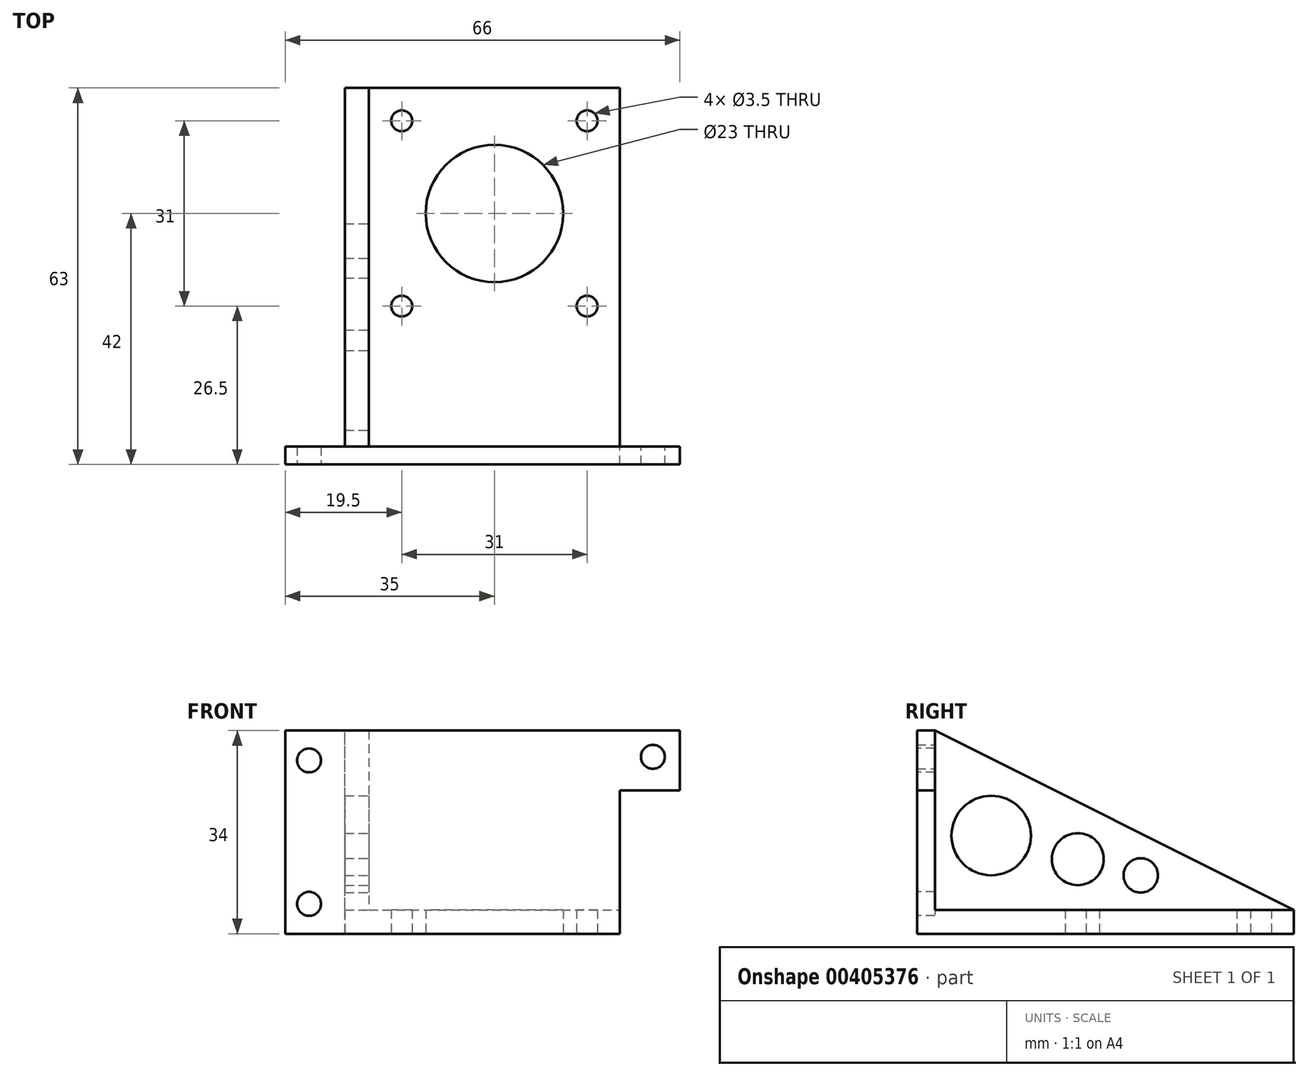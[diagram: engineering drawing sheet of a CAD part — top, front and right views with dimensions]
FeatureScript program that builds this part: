
annotation { "Feature Type Name" : "Feature", "Feature Type Description" : "" }
export const myFeature = defineFeature(function(context is Context, id is Id, definition is map)
    precondition{}
    {
        {
            var Q0;
            Q0=qCreatedBy(makeId("Top.planeOp"),FACE);
            var sketch = newSketch(context, id + "F0", { "sketchPlane" : qUnion([Q0])});
            skLineSegment(sketch, "E0.bottom", {"start": v(-21, 31.5) * mm, "end": v(21, 31.5) * mm});
            skLineSegment(sketch, "E0.top", {"start": v(-21, -31.5) * mm, "end": v(21, -31.5) * mm});
            skLineSegment(sketch, "E0.left", {"start": v(-21, 31.5) * mm, "end": v(-21, -31.5) * mm});
            skLineSegment(sketch, "E0.right", {"start": v(21, 31.5) * mm, "end": v(21, -31.5) * mm});
            skPoint(sketch, "E0.middle", {"position": v(0, 0) * mm});
            skCircle(sketch, "E1", {"center": v(0, 10.5) * mm, "radius": 11.5 * mm});
            skCircle(sketch, "E2", {"center": v(-15.5, 26) * mm, "radius": 1.75 * mm});
            skCircle(sketch, "E3.1.0", {"center": v(-15.5, -5) * mm, "radius": 1.75 * mm});
            skCircle(sketch, "E3.2.0", {"center": v(15.5, -5) * mm, "radius": 1.75 * mm});
            skCircle(sketch, "E3.3.0", {"center": v(15.5, 26) * mm, "radius": 1.75 * mm});
            skSolve(sketch);
        }
        {
            var Q0;
            Q0=makeQuery(id+"F0.imprint","IMPRINT",FACE,{"disambiguationData":[TD([[makeQuery(id+"F0.imprint","IMPRINT",EDGE,{"derivedFrom":sQuery(id+"F0.wireOp",EDGE,"E0.bottom")}),-1.0]])]});
            extrude(context, id + "F1", {"entities" : qUnion([Q0]), "depth" : 4 * mm});
        }
        {
            var Q0;
            Q0=makeQuery(id+"F1.opExtrude","CAP_FACE",FACE,{"disambiguationData":[OSD([sQuery(id+"F0.wireOp",EDGE,"E0.bottom"),sQuery(id+"F0.wireOp",EDGE,"E0.top"),sQuery(id+"F0.wireOp",EDGE,"E0.left"),sQuery(id+"F0.wireOp",EDGE,"E0.right"),sQuery(id+"F0.wireOp",EDGE,"E1"),sQuery(id+"F0.wireOp",EDGE,"E2"),sQuery(id+"F0.wireOp",EDGE,"E3.1.0"),sQuery(id+"F0.wireOp",EDGE,"E3.2.0"),sQuery(id+"F0.wireOp",EDGE,"E3.3.0")])],"isStart":false});
            var sketch = newSketch(context, id + "F2", { "sketchPlane" : qUnion([Q0])});
            skLineSegment(sketch, "E4.bottom", {"start": v(-21, -31.5) * mm, "end": v(21, -31.5) * mm});
            skLineSegment(sketch, "E4.top", {"start": v(-21, -28.5) * mm, "end": v(21, -28.5) * mm});
            skLineSegment(sketch, "E4.left", {"start": v(-21, -31.5) * mm, "end": v(-21, -28.5) * mm});
            skLineSegment(sketch, "E4.right", {"start": v(21, -31.5) * mm, "end": v(21, -28.5) * mm});
            skSolve(sketch);
        }
        {
            var Q0;
            Q0=makeQuery(id+"F2.imprint","IMPRINT",FACE,{"disambiguationData":[TD([[makeQuery(id+"F2.imprint","IMPRINT",EDGE,{"derivedFrom":sQuery(id+"F2.wireOp",EDGE,"E4.bottom")}),1.0]])]});
            extrude(context, id + "F3", {"entities" : qUnion([Q0]), "operationType" : NewBodyOperationType.ADD, "depth" : 30 * mm});
        }
        {
            var Q0;
            Q0=makeQuery(id+"F3.boolean.opBoolean","MERGE",FACE,{"derivedFrom":[makeQuery(id+"F1.opExtrude","SWEPT_FACE",FACE,{"disambiguationData":[OSD([sQuery(id+"F0.wireOp",EDGE,"E0.left")])]}),makeQuery(id+"F3.opExtrude","SWEPT_FACE",FACE,{"disambiguationData":[OSD([sQuery(id+"F2.wireOp",EDGE,"E4.left")])]})]});
            var sketch = newSketch(context, id + "F4", { "sketchPlane" : qUnion([Q0])});
            skLineSegment(sketch, "E5", {"start": v(-31.5, 4) * mm, "end": v(28.5, 34) * mm});
            skLineSegment(sketch, "E6", {"start": v(28.5, 34) * mm, "end": v(31.5, 34) * mm});
            skLineSegment(sketch, "E7", {"start": v(31.5, 34) * mm, "end": v(31.5, 0) * mm});
            skLineSegment(sketch, "E8", {"start": v(31.5, 0) * mm, "end": v(-31.5, 0) * mm});
            skLineSegment(sketch, "E9", {"start": v(-31.5, 0) * mm, "end": v(-31.5, 4) * mm});
            skCircle(sketch, "E10", {"center": v(19.1, 16.43) * mm, "radius": 6.65 * mm});
            skCircle(sketch, "E11", {"center": v(4.62, 12.47) * mm, "radius": 4.34 * mm});
            skCircle(sketch, "E12", {"center": v(-5.9, 9.76) * mm, "radius": 2.88 * mm});
            skSolve(sketch);
        }
        {
            var Q0;
            Q0=makeQuery(id+"F4.imprint","IMPRINT",FACE,{"disambiguationData":[TD([[makeQuery(id+"F4.imprint","IMPRINT",EDGE,{"derivedFrom":sQuery(id+"F4.wireOp",EDGE,"E5")}),-1.0]])]});
            var Q1;
            Q1=makeQuery(id+"F4.imprint","IMPRINT",FACE,{"disambiguationData":[TD([[makeQuery(id+"F4.imprint","IMPRINT",EDGE,{"derivedFrom":sQuery(id+"F4.wireOp",EDGE,"E6")}),-1.0]])]});
            extrude(context, id + "F5", {"entities" : qUnion([Q0, Q1]), "operationType" : NewBodyOperationType.ADD, "depth" : 4 * mm});
        }
        {
            var Q0;
            Q0=makeQuery(id+"F3.boolean.opBoolean","MERGE",FACE,{"derivedFrom":[makeQuery(id+"F1.opExtrude","SWEPT_FACE",FACE,{"disambiguationData":[OSD([sQuery(id+"F0.wireOp",EDGE,"E0.right")])]}),makeQuery(id+"F3.opExtrude","SWEPT_FACE",FACE,{"disambiguationData":[OSD([sQuery(id+"F2.wireOp",EDGE,"E4.right")])]})]});
            var sketch = newSketch(context, id + "F6", { "sketchPlane" : qUnion([Q0])});
            skLineSegment(sketch, "E13.bottom", {"start": v(-31.5, 34) * mm, "end": v(-28.5, 34) * mm});
            skLineSegment(sketch, "E13.top", {"start": v(-31.5, 24) * mm, "end": v(-28.5, 24) * mm});
            skLineSegment(sketch, "E13.left", {"start": v(-31.5, 34) * mm, "end": v(-31.5, 24) * mm});
            skLineSegment(sketch, "E13.right", {"start": v(-28.5, 34) * mm, "end": v(-28.5, 24) * mm});
            skSolve(sketch);
        }
        {
            var Q0;
            Q0=makeQuery(id+"F6.imprint","IMPRINT",FACE,{"disambiguationData":[TD([[makeQuery(id+"F6.imprint","IMPRINT",EDGE,{"derivedFrom":sQuery(id+"F6.wireOp",EDGE,"E13.bottom")}),1.0]])]});
            extrude(context, id + "F7", {"entities" : qUnion([Q0]), "operationType" : NewBodyOperationType.ADD, "depth" : 10 * mm});
        }
        {
            var Q0;
            Q0=makeQuery(id+"F7.boolean.opBoolean","MERGE",FACE,{"derivedFrom":[makeQuery(id+"F3.opExtrude","SWEPT_FACE",FACE,{"disambiguationData":[OSD([sQuery(id+"F2.wireOp",EDGE,"E4.top")])]}),makeQuery(id+"F7.opExtrude","SWEPT_FACE",FACE,{"disambiguationData":[OSD([sQuery(id+"F6.wireOp",EDGE,"E13.right")])]})]});
            var sketch = newSketch(context, id + "F8", { "sketchPlane" : qUnion([Q0])});
            skCircle(sketch, "E14", {"center": v(-26.5, 29.6) * mm, "radius": 2 * mm});
            skSolve(sketch);
        }
        {
            var Q0;
            Q0=makeQuery(id+"F8.imprint","IMPRINT",FACE,{"disambiguationData":[TD([[makeQuery(id+"F8.imprint","IMPRINT",EDGE,{"derivedFrom":sQuery(id+"F8.wireOp",EDGE,"E14")}),1.0]])]});
            extrude(context, id + "F9", {"entities" : qUnion([Q0]), "operationType" : NewBodyOperationType.REMOVE, "oppositeDirection" : true, "depth" : 25 * mm});
        }
        {
            var Q0;
            Q0=makeQuery(id+"F5.opExtrude","CAP_FACE",FACE,{"disambiguationData":[OSD([sQuery(id+"F4.wireOp",EDGE,"E5"),sQuery(id+"F4.wireOp",EDGE,"E6"),sQuery(id+"F4.wireOp",EDGE,"E7"),sQuery(id+"F4.wireOp",EDGE,"E8"),sQuery(id+"F4.wireOp",EDGE,"E9"),sQuery(id+"F4.wireOp",EDGE,"E10"),sQuery(id+"F4.wireOp",EDGE,"E11"),sQuery(id+"F4.wireOp",EDGE,"E12")])],"isStart":false});
            var sketch = newSketch(context, id + "F10", { "sketchPlane" : qUnion([Q0])});
            skLineSegment(sketch, "E15.bottom", {"start": v(31.5, 0) * mm, "end": v(28.5, 0) * mm});
            skLineSegment(sketch, "E15.top", {"start": v(31.5, 34) * mm, "end": v(28.5, 34) * mm});
            skLineSegment(sketch, "E15.left", {"start": v(31.5, 0) * mm, "end": v(31.5, 34) * mm});
            skLineSegment(sketch, "E15.right", {"start": v(28.5, 0) * mm, "end": v(28.5, 34) * mm});
            skSolve(sketch);
        }
        {
            var Q0;
            Q0=makeQuery(id+"F10.imprint","IMPRINT",FACE,{"disambiguationData":[TD([[makeQuery(id+"F10.imprint","IMPRINT",EDGE,{"derivedFrom":sQuery(id+"F10.wireOp",EDGE,"E15.bottom")}),1.0]])]});
            extrude(context, id + "F11", {"entities" : qUnion([Q0]), "operationType" : NewBodyOperationType.ADD, "depth" : 10 * mm});
        }
        {
            var Q0;
            Q0=makeQuery(id+"F11.boolean.opBoolean","MERGE",FACE,{"derivedFrom":[makeQuery(id+"F7.boolean.opBoolean","MERGE",FACE,{"derivedFrom":[makeQuery(id+"F5.boolean.opBoolean","MERGE",FACE,{"derivedFrom":[makeQuery(id+"F3.boolean.opBoolean","MERGE",FACE,{"derivedFrom":[makeQuery(id+"F1.opExtrude","SWEPT_FACE",FACE,{"disambiguationData":[OSD([sQuery(id+"F0.wireOp",EDGE,"E0.top")])]}),makeQuery(id+"F3.opExtrude","SWEPT_FACE",FACE,{"disambiguationData":[OSD([sQuery(id+"F2.wireOp",EDGE,"E4.bottom")])]})]}),makeQuery(id+"F5.opExtrude","SWEPT_FACE",FACE,{"disambiguationData":[OSD([sQuery(id+"F4.wireOp",EDGE,"E7")])]})]}),makeQuery(id+"F7.opExtrude","SWEPT_FACE",FACE,{"disambiguationData":[OSD([sQuery(id+"F6.wireOp",EDGE,"E13.left")])]})]}),makeQuery(id+"F11.opExtrude","SWEPT_FACE",FACE,{"disambiguationData":[OSD([sQuery(id+"F10.wireOp",EDGE,"E15.left")])]})]});
            var sketch = newSketch(context, id + "F12", { "sketchPlane" : qUnion([Q0])});
            skCircle(sketch, "E16", {"center": v(-31, 29) * mm, "radius": 2 * mm});
            skCircle(sketch, "E17", {"center": v(-31, 5) * mm, "radius": 2 * mm});
            skSolve(sketch);
        }
        {
            var Q0;
            Q0=makeQuery(id+"F12.imprint","IMPRINT",FACE,{"disambiguationData":[TD([[makeQuery(id+"F12.imprint","IMPRINT",EDGE,{"derivedFrom":sQuery(id+"F12.wireOp",EDGE,"E16")}),1.0]])]});
            var Q1;
            Q1=makeQuery(id+"F12.imprint","IMPRINT",FACE,{"disambiguationData":[TD([[makeQuery(id+"F12.imprint","IMPRINT",EDGE,{"derivedFrom":sQuery(id+"F12.wireOp",EDGE,"E17")}),1.0]])]});
            extrude(context, id + "F13", {"entities" : qUnion([Q0, Q1]), "operationType" : NewBodyOperationType.REMOVE, "oppositeDirection" : true, "depth" : 25 * mm});
        }
    });
